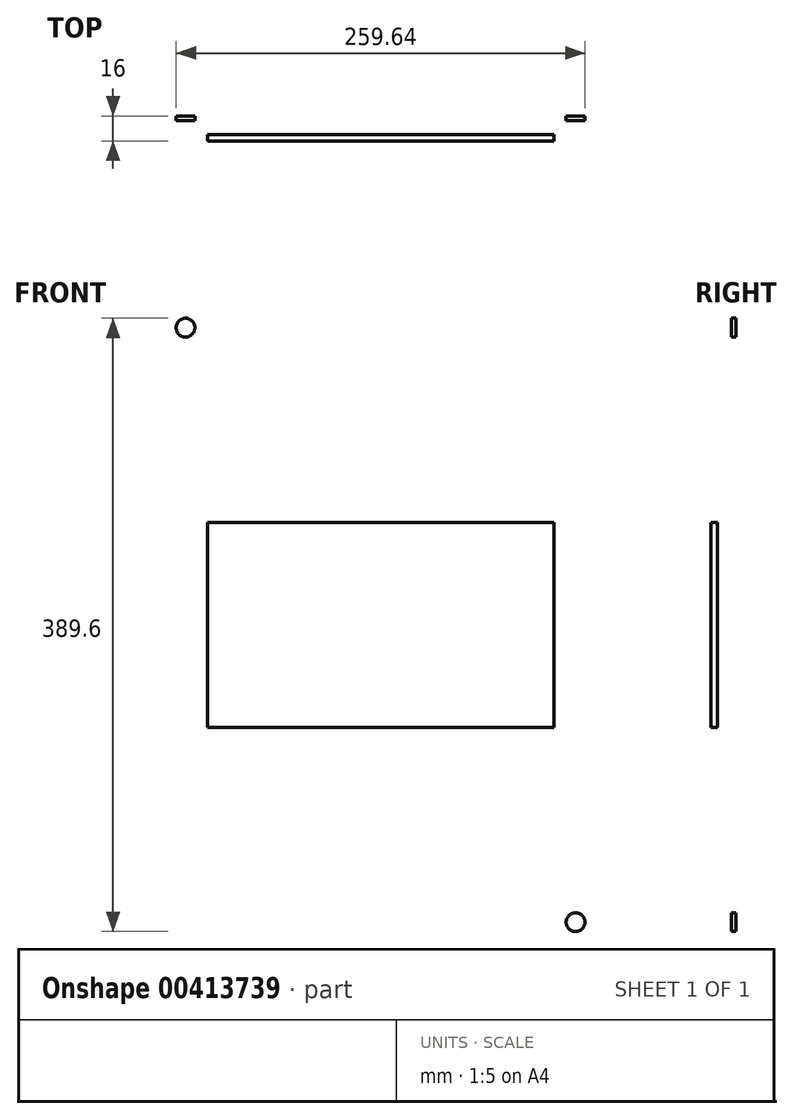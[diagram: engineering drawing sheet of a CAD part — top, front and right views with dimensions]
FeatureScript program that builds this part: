
annotation { "Feature Type Name" : "Feature", "Feature Type Description" : "" }
export const myFeature = defineFeature(function(context is Context, id is Id, definition is map)
    precondition{}
    {
        {
            var Q0;
            Q0=qCreatedBy(makeId("Front.planeOp"),FACE);
            var sketch = newSketch(context, id + "F0", { "sketchPlane" : qUnion([Q0])});
            skLineSegment(sketch, "E0.bottom", {"start": v(137, -200) * mm, "end": v(-137, -200) * mm});
            skLineSegment(sketch, "E0.top", {"start": v(137, 200) * mm, "end": v(-137, 200) * mm});
            skLineSegment(sketch, "E0.left", {"start": v(137, -200) * mm, "end": v(137, 200) * mm});
            skLineSegment(sketch, "E0.right", {"start": v(-137, -200) * mm, "end": v(-137, 200) * mm});
            skPoint(sketch, "E0.middle", {"position": v(0, 0) * mm});
            skSolve(sketch);
        }
        {
            var Q0;
            Q0=makeQuery(id+"F0.imprint","IMPRINT",FACE,{"disambiguationData":[TD([[makeQuery(id+"F0.imprint","IMPRINT",EDGE,{"derivedFrom":sQuery(id+"F0.wireOp",EDGE,"E0.bottom")}),-1.0]])]});
            var sketch = newSketch(context, id + "F1", { "sketchPlane" : qUnion([Q0])});
            skLineSegment(sketch, "E1.bottom", {"start": v(128.5, -87) * mm, "end": v(-128.5, -87) * mm});
            skLineSegment(sketch, "E1.top", {"start": v(128.5, 87) * mm, "end": v(-128.5, 87) * mm});
            skLineSegment(sketch, "E1.left", {"start": v(128.5, -87) * mm, "end": v(128.5, 87) * mm});
            skLineSegment(sketch, "E1.right", {"start": v(-128.5, -87) * mm, "end": v(-128.5, 87) * mm});
            skPoint(sketch, "E1.middle", {"position": v(0, 0) * mm});
            skSolve(sketch);
        }
        {
            var Q0;
            Q0=makeQuery(id+"F0.imprint","IMPRINT",FACE,{"disambiguationData":[TD([[makeQuery(id+"F0.imprint","IMPRINT",EDGE,{"derivedFrom":sQuery(id+"F0.wireOp",EDGE,"E0.bottom")}),-1.0]])]});
            extrude(context, id + "F2", {"entities" : qUnion([Q0]), "depth" : 13 * mm});
        }
        {
            var Q0;
            Q0=makeQuery(id+"F1.imprint","IMPRINT",FACE,{"disambiguationData":[TD([[makeQuery(id+"F1.imprint","IMPRINT",EDGE,{"derivedFrom":sQuery(id+"F1.wireOp",EDGE,"E1.bottom")}),-1.0]])]});
            extrude(context, id + "F3", {"entities" : qUnion([Q0]), "operationType" : NewBodyOperationType.REMOVE, "depth" : 9 * mm});
        }
        {
            var Q0;
            Q0=makeQuery(id+"F2.opExtrude","CAP_FACE",FACE,{"disambiguationData":[OSD([sQuery(id+"F0.wireOp",EDGE,"E0.bottom"),sQuery(id+"F0.wireOp",EDGE,"E0.top"),sQuery(id+"F0.wireOp",EDGE,"E0.left"),sQuery(id+"F0.wireOp",EDGE,"E0.right")])],"isStart":true});
            var sketch = newSketch(context, id + "F4", { "sketchPlane" : qUnion([Q0])});
            skLineSegment(sketch, "E2.bottom", {"start": v(-137, 200) * mm, "end": v(137, 200) * mm});
            skLineSegment(sketch, "E2.top", {"start": v(-137, -200) * mm, "end": v(137, -200) * mm});
            skLineSegment(sketch, "E2.left", {"start": v(-137, 200) * mm, "end": v(-137, -200) * mm});
            skLineSegment(sketch, "E2.right", {"start": v(137, 200) * mm, "end": v(137, -200) * mm});
            skLineSegment(sketch, "E3.bottom", {"start": v(110, -65) * mm, "end": v(-110, -65) * mm});
            skLineSegment(sketch, "E3.top", {"start": v(110, 65) * mm, "end": v(-110, 65) * mm});
            skLineSegment(sketch, "E3.left", {"start": v(110, -65) * mm, "end": v(110, 65) * mm});
            skLineSegment(sketch, "E3.right", {"start": v(-110, -65) * mm, "end": v(-110, 65) * mm});
            skPoint(sketch, "E3.middle", {"position": v(0, 0) * mm});
            skSolve(sketch);
        }
        {
            var Q0;
            Q0 = qSketchRegion(id + "F4", true);
            extrude(context, id + "F5", {"entities" : qUnion([Q0]), "depth" : 3 * mm});
        }
        {
            var Q0;
            Q0=makeQuery(id+"F3.boolean.opBoolean","COPY",FACE,{"derivedFrom":makeQuery(id+"F3.opExtrude","CAP_FACE",FACE,{"disambiguationData":[OSD([sQuery(id+"F1.wireOp",EDGE,"E1.bottom"),sQuery(id+"F1.wireOp",EDGE,"E1.top"),sQuery(id+"F1.wireOp",EDGE,"E1.left"),sQuery(id+"F1.wireOp",EDGE,"E1.right")])],"isStart":false})});
            var sketch = newSketch(context, id + "F6", { "sketchPlane" : qUnion([Q0])});
            skLineSegment(sketch, "E4.bottom", {"start": v(-136.73, 105.76) * mm, "end": v(135.97, 105.76) * mm});
            skLineSegment(sketch, "E4.top", {"start": v(-136.73, -101.98) * mm, "end": v(135.97, -101.98) * mm});
            skLineSegment(sketch, "E4.left", {"start": v(-136.73, 105.76) * mm, "end": v(-136.73, -101.98) * mm});
            skLineSegment(sketch, "E4.right", {"start": v(135.97, 105.76) * mm, "end": v(135.97, -101.98) * mm});
            skSolve(sketch);
        }
        {
            var Q0;
            Q0 = qSketchRegion(id + "F6", true);
            extrude(context, id + "F7", {"entities" : qUnion([Q0]), "depth" : 3 * mm});
        }
        {
            var Q0;
            Q0=makeQuery(id+"F7.opExtrude","SWEPT_BODY",BODY,{"disambiguationData":[OSD([sQuery(id+"F6.wireOp",EDGE,"E4.bottom"),sQuery(id+"F6.wireOp",EDGE,"E4.top"),sQuery(id+"F6.wireOp",EDGE,"E4.left"),sQuery(id+"F6.wireOp",EDGE,"E4.right")])]});
            deleteBodies(context, id + "F8", {"entities" : qUnion([Q0])});
        }
        {
            var Q0;
            Q0=makeQuery(id+"F2.opExtrude","CAP_FACE",FACE,{"disambiguationData":[OSD([sQuery(id+"F0.wireOp",EDGE,"E0.bottom"),sQuery(id+"F0.wireOp",EDGE,"E0.top"),sQuery(id+"F0.wireOp",EDGE,"E0.left"),sQuery(id+"F0.wireOp",EDGE,"E0.right")])],"isStart":false});
            var sketch = newSketch(context, id + "F9", { "sketchPlane" : qUnion([Q0])});
            skLineSegment(sketch, "E5", {"start": v(-13.5, -85.8) * mm, "end": v(-13.5, -115.8) * mm});
            skLineSegment(sketch, "E6", {"start": v(-13.5, -115.8) * mm, "end": v(21.5, -115.8) * mm});
            skLineSegment(sketch, "E7", {"start": v(21.5, -115.8) * mm, "end": v(21.5, -85.8) * mm});
            skLineSegment(sketch, "E8", {"start": v(21.5, -85.8) * mm, "end": v(-13.5, -85.8) * mm});
            skSolve(sketch);
        }
        {
            var Q0;
            Q0=makeQuery(id+"F9.imprint","IMPRINT",FACE,{"disambiguationData":[TD([[makeQuery(id+"F9.imprint","IMPRINT",EDGE,{"derivedFrom":sQuery(id+"F9.wireOp",EDGE,"E5")}),1.0]])]});
            extrude(context, id + "F10", {"entities" : qUnion([Q0]), "operationType" : NewBodyOperationType.REMOVE, "oppositeDirection" : true, "depth" : 13 * mm});
        }
        {
            var Q0;
            Q0=makeQuery(id+"F2.opExtrude","CAP_FACE",FACE,{"disambiguationData":[OSD([sQuery(id+"F0.wireOp",EDGE,"E0.bottom"),sQuery(id+"F0.wireOp",EDGE,"E0.top"),sQuery(id+"F0.wireOp",EDGE,"E0.left"),sQuery(id+"F0.wireOp",EDGE,"E0.right")])],"isStart":true});
            var sketch = newSketch(context, id + "F11", { "sketchPlane" : qUnion([Q0])});
            skLineSegment(sketch, "E9", {"start": v(-107, 87) * mm, "end": v(-107, 112) * mm});
            skLineSegment(sketch, "E10", {"start": v(-107, 112) * mm, "end": v(-37, 112) * mm});
            skLineSegment(sketch, "E11", {"start": v(-37, 112) * mm, "end": v(-37, 87) * mm});
            skLineSegment(sketch, "E12", {"start": v(-37, 87) * mm, "end": v(-107, 87) * mm});
            skSolve(sketch);
        }
        {
            var Q0;
            Q0=makeQuery(id+"F11.imprint","IMPRINT",FACE,{"disambiguationData":[TD([[makeQuery(id+"F11.imprint","IMPRINT",EDGE,{"derivedFrom":sQuery(id+"F11.wireOp",EDGE,"E9")}),-1.0]])]});
            extrude(context, id + "F12", {"entities" : qUnion([Q0]), "operationType" : NewBodyOperationType.REMOVE, "oppositeDirection" : true, "depth" : 13 * mm});
        }
        {
            var Q0;
            Q0=makeQuery(id+"F5.opExtrude","CAP_FACE",FACE,{"disambiguationData":[OSD([sQuery(id+"F4.wireOp",EDGE,"E2.bottom"),sQuery(id+"F4.wireOp",EDGE,"E2.top"),sQuery(id+"F4.wireOp",EDGE,"E2.left"),sQuery(id+"F4.wireOp",EDGE,"E2.right"),sQuery(id+"F4.wireOp",EDGE,"E3.bottom"),sQuery(id+"F4.wireOp",EDGE,"E3.top"),sQuery(id+"F4.wireOp",EDGE,"E3.left"),sQuery(id+"F4.wireOp",EDGE,"E3.right")])],"isStart":false});
            var sketch = newSketch(context, id + "F13", { "sketchPlane" : qUnion([Q0])});
            skCircle(sketch, "E13", {"center": v(-123.85, 188.83) * mm, "radius": 5.97 * mm});
            skLineSegment(sketch, "E14", {"start": v(0, 200) * mm, "end": v(0, -200) * mm, "construction": true});
            skLineSegment(sketch, "E15", {"start": v(-137, 0) * mm, "end": v(137, 0) * mm, "construction": true});
            skCircle(sketch, "E16.MirrorC", {"center": v(123.85, 188.83) * mm, "radius": 5.97 * mm});
            skCircle(sketch, "E17.MirrorC", {"center": v(-123.85, -188.83) * mm, "radius": 5.97 * mm});
            skCircle(sketch, "E18.MirrorC", {"center": v(123.85, -188.83) * mm, "radius": 5.97 * mm});
            skSolve(sketch);
        }
        {
            var Q0;
            Q0=makeQuery(id+"F13.imprint","IMPRINT",FACE,{"disambiguationData":[TD([[makeQuery(id+"F13.imprint","IMPRINT",EDGE,{"derivedFrom":sQuery(id+"F13.wireOp",EDGE,"E13")}),1.0]])]});
            extrude(context, id + "F14", {"entities" : qUnion([Q0]), "operationType" : NewBodyOperationType.REMOVE, "endBound" : BoundingType.THROUGH_ALL, "oppositeDirection" : true, "depth" : 20 * mm});
        }
        {
            var Q0;
            Q0=makeQuery(id+"F13.imprint","IMPRINT",FACE,{"disambiguationData":[TD([[makeQuery(id+"F13.imprint","IMPRINT",EDGE,{"derivedFrom":sQuery(id+"F13.wireOp",EDGE,"E16.MirrorC")}),-1.0]])]});
            extrude(context, id + "F15", {"entities" : qUnion([Q0]), "operationType" : NewBodyOperationType.REMOVE, "oppositeDirection" : true, "depth" : 25 * mm});
        }
        {
            var Q0;
            Q0=makeQuery(id+"F13.imprint","IMPRINT",FACE,{"disambiguationData":[TD([[makeQuery(id+"F13.imprint","IMPRINT",EDGE,{"derivedFrom":sQuery(id+"F13.wireOp",EDGE,"E17.MirrorC")}),-1.0]])]});
            extrude(context, id + "F16", {"entities" : qUnion([Q0]), "operationType" : NewBodyOperationType.REMOVE, "oppositeDirection" : true, "depth" : 25 * mm});
        }
        {
            var Q0;
            Q0=makeQuery(id+"F13.imprint","IMPRINT",FACE,{"disambiguationData":[TD([[makeQuery(id+"F13.imprint","IMPRINT",EDGE,{"derivedFrom":sQuery(id+"F13.wireOp",EDGE,"E18.MirrorC")}),1.0]])]});
            extrude(context, id + "F17", {"entities" : qUnion([Q0]), "operationType" : NewBodyOperationType.REMOVE, "oppositeDirection" : true, "depth" : 25 * mm});
        }
        {
            var Q0;
            Q0=makeQuery(id+"F2.opExtrude","CAP_FACE",FACE,{"disambiguationData":[OSD([sQuery(id+"F0.wireOp",EDGE,"E0.bottom"),sQuery(id+"F0.wireOp",EDGE,"E0.top"),sQuery(id+"F0.wireOp",EDGE,"E0.left"),sQuery(id+"F0.wireOp",EDGE,"E0.right")])],"isStart":true});
            var sketch = newSketch(context, id + "F18", { "sketchPlane" : qUnion([Q0])});
            skLineSegment(sketch, "E19.bottom", {"start": v(-137, 200) * mm, "end": v(137, 200) * mm});
            skLineSegment(sketch, "E19.top", {"start": v(-137, 150) * mm, "end": v(137, 150) * mm});
            skLineSegment(sketch, "E19.left", {"start": v(-137, 200) * mm, "end": v(-137, 150) * mm});
            skLineSegment(sketch, "E19.right", {"start": v(137, 200) * mm, "end": v(137, 150) * mm});
            skLineSegment(sketch, "E20.bottom", {"start": v(-137, -150) * mm, "end": v(137, -150) * mm});
            skLineSegment(sketch, "E20.top", {"start": v(-137, -200) * mm, "end": v(137, -200) * mm});
            skLineSegment(sketch, "E20.left", {"start": v(-137, -150) * mm, "end": v(-137, -200) * mm});
            skLineSegment(sketch, "E20.right", {"start": v(137, -150) * mm, "end": v(137, -200) * mm});
            skSolve(sketch);
        }
        {
            var Q0;
            Q0 = qSketchRegion(id + "F18", true);
            extrude(context, id + "F19", {"entities" : qUnion([Q0]), "operationType" : NewBodyOperationType.REMOVE, "endBound" : BoundingType.THROUGH_ALL, "oppositeDirection" : true, "depth" : 25 * mm});
        }
    });
